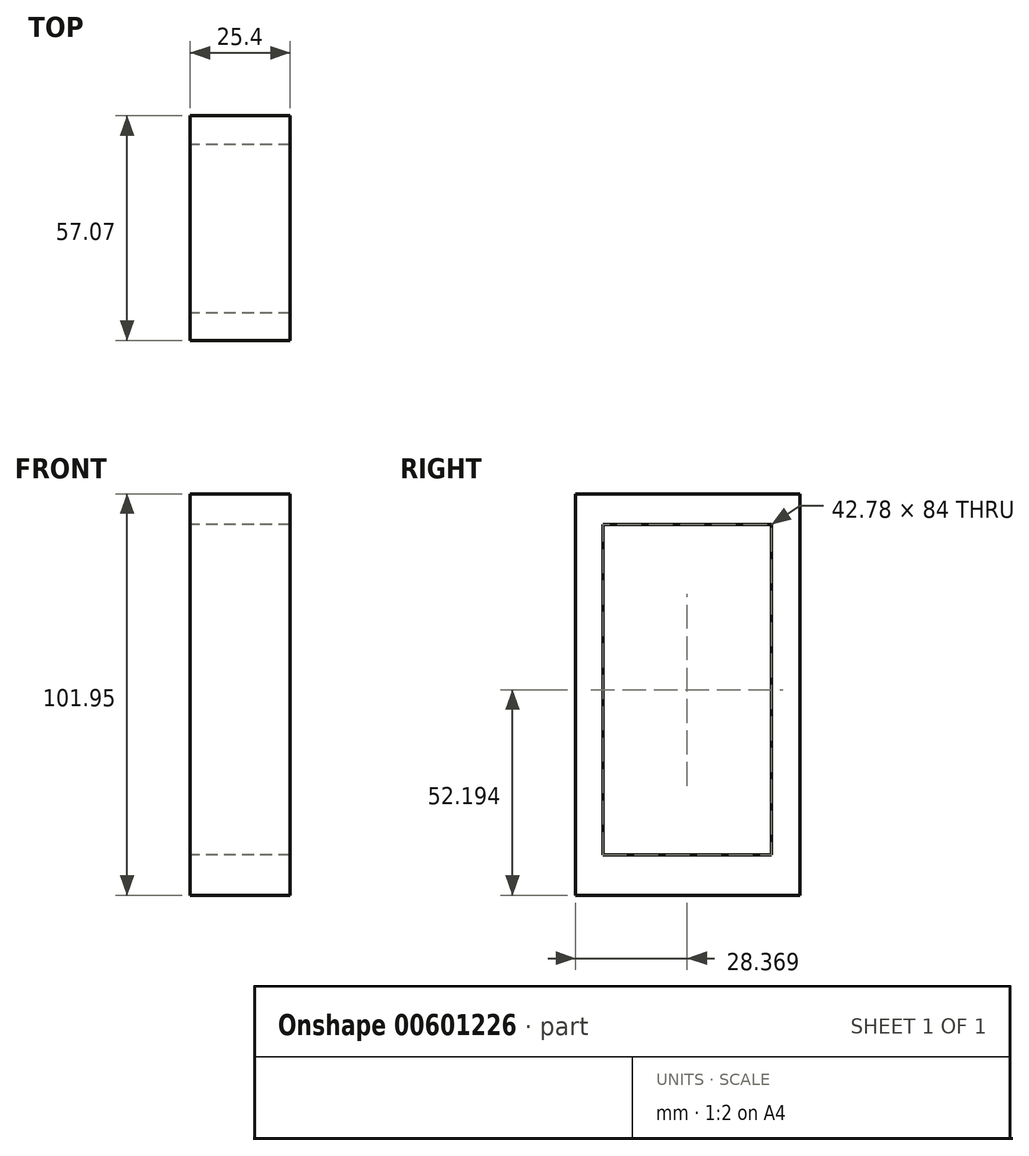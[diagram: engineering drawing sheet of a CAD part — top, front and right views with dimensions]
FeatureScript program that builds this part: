
annotation { "Feature Type Name" : "Feature", "Feature Type Description" : "" }
export const myFeature = defineFeature(function(context is Context, id is Id, definition is map)
    precondition{}
    {
        {
            var Q0;
            Q0=qCreatedBy(makeId("Right.planeOp"),FACE);
            var sketch = newSketch(context, id + "F0", { "sketchPlane" : qUnion([Q0])});
            skLineSegment(sketch, "E0.bottom", {"start": v(0, 34.02) * mm, "end": v(57.07, 34.02) * mm});
            skLineSegment(sketch, "E0.top", {"start": v(0, -67.93) * mm, "end": v(57.07, -67.93) * mm});
            skLineSegment(sketch, "E0.left", {"start": v(0, 34.02) * mm, "end": v(0, -67.93) * mm});
            skLineSegment(sketch, "E0.right", {"start": v(57.07, 34.02) * mm, "end": v(57.07, -67.93) * mm});
            skLineSegment(sketch, "E1.bottom", {"start": v(6.98, 26.26) * mm, "end": v(49.76, 26.26) * mm});
            skLineSegment(sketch, "E1.top", {"start": v(6.98, -57.74) * mm, "end": v(49.76, -57.74) * mm});
            skLineSegment(sketch, "E1.left", {"start": v(6.98, 26.26) * mm, "end": v(6.98, -57.74) * mm});
            skLineSegment(sketch, "E1.right", {"start": v(49.76, 26.26) * mm, "end": v(49.76, -57.74) * mm});
            skSolve(sketch);
        }
        {
            var Q0;
            Q0 = qSketchRegion(id + "F0", true);
            extrude(context, id + "F1", {"entities" : qUnion([Q0]), "depth" : 25.4 * mm, "offsetDistance" : 25.4 * mm});
        }
    });
